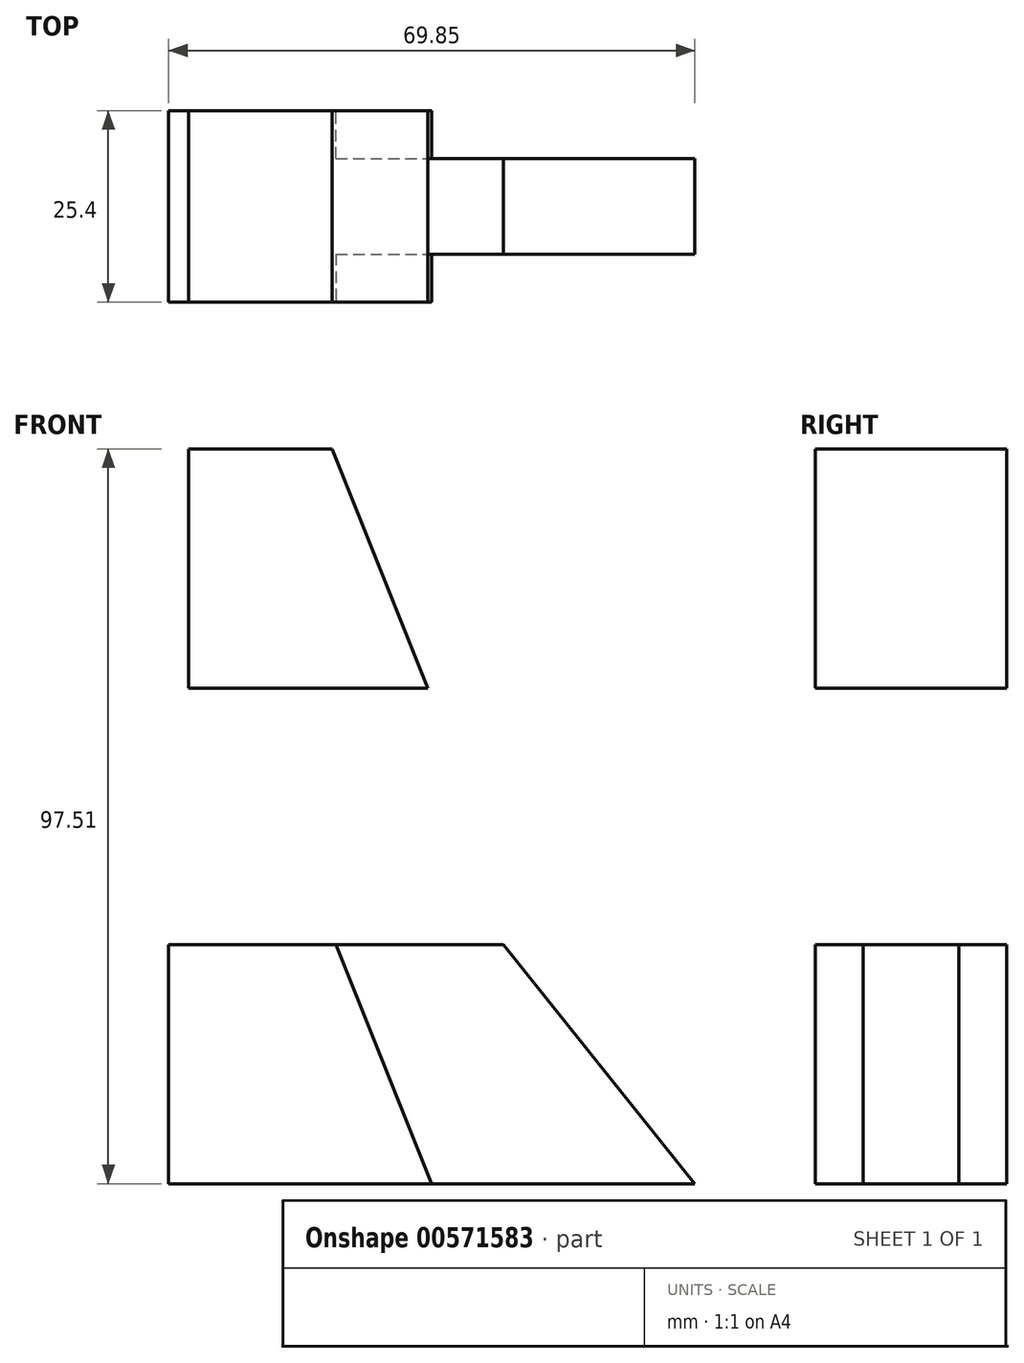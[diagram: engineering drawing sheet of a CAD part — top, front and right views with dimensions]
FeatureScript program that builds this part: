
annotation { "Feature Type Name" : "Feature", "Feature Type Description" : "" }
export const myFeature = defineFeature(function(context is Context, id is Id, definition is map)
    precondition{}
    {
        {
            var Q0;
            Q0=qCreatedBy(makeId("Front.planeOp"),FACE);
            var sketch = newSketch(context, id + "F0", { "sketchPlane" : qUnion([Q0])});
            skLineSegment(sketch, "E0", {"start": v(-62.13, 47.31) * mm, "end": v(-62.13, 15.56) * mm});
            skLineSegment(sketch, "E1", {"start": v(-62.13, 15.56) * mm, "end": v(-30.38, 15.56) * mm});
            skLineSegment(sketch, "E2", {"start": v(-62.13, 47.31) * mm, "end": v(-43.08, 47.31) * mm});
            skLineSegment(sketch, "E3", {"start": v(-43.08, 47.31) * mm, "end": v(-30.38, 15.56) * mm});
            skSolve(sketch);
        }
        {
            var Q0;
            Q0=makeQuery(id+"F0.imprint","IMPRINT",FACE,{"disambiguationData":[TD([[makeQuery(id+"F0.imprint","IMPRINT",EDGE,{"derivedFrom":sQuery(id+"F0.wireOp",EDGE,"E0")}),1.0]])]});
            extrude(context, id + "F1", {"entities" : qUnion([Q0]), "depth" : 25.4 * mm, "offsetDistance" : 25.4 * mm});
        }
        {
            var Q0;
            Q0=qCreatedBy(makeId("Front.planeOp"),FACE);
            var sketch = newSketch(context, id + "F2", { "sketchPlane" : qUnion([Q0])});
            skLineSegment(sketch, "E4", {"start": v(-64.78, -18.45) * mm, "end": v(-64.78, -50.2) * mm});
            skLineSegment(sketch, "E5", {"start": v(-64.78, -18.45) * mm, "end": v(-20.33, -18.45) * mm});
            skLineSegment(sketch, "E6", {"start": v(-64.78, -50.2) * mm, "end": v(5.07, -50.2) * mm});
            skLineSegment(sketch, "E7", {"start": v(-20.33, -18.45) * mm, "end": v(5.07, -50.2) * mm});
            skSolve(sketch);
        }
        {
            var Q0;
            Q0=makeQuery(id+"F2.imprint","IMPRINT",FACE,{"disambiguationData":[TD([[makeQuery(id+"F2.imprint","IMPRINT",EDGE,{"derivedFrom":sQuery(id+"F2.wireOp",EDGE,"E4")}),1.0]])]});
            extrude(context, id + "F3", {"entities" : qUnion([Q0]), "depth" : 25.4 * mm, "offsetDistance" : 25.4 * mm});
        }
        {
            var Q0;
            Q0=makeQuery(id+"F3.opExtrude","CAP_FACE",FACE,{"disambiguationData":[OSD([sQuery(id+"F2.wireOp",EDGE,"E4"),sQuery(id+"F2.wireOp",EDGE,"E5"),sQuery(id+"F2.wireOp",EDGE,"E6"),sQuery(id+"F2.wireOp",EDGE,"E7")])],"isStart":false});
            var sketch = newSketch(context, id + "F4", { "sketchPlane" : qUnion([Q0])});
            skLineSegment(sketch, "E8", {"start": v(-42.56, -18.45) * mm, "end": v(-29.86, -50.2) * mm});
            skSolve(sketch);
        }
        {
            var Q0;
            {var subQ0=sQuery(id+"F4.wireOp",EDGE,"E8");Q0=makeQuery(id+"F4.imprint","IMPRINT",FACE,{"disambiguationData":[TD([[makeQuery(id+"F4.imprint","IMPRINT",EDGE,{"derivedFrom":subQ0}),1.0]])]});}
            extrude(context, id + "F5", {"entities" : qUnion([Q0]), "operationType" : NewBodyOperationType.REMOVE, "oppositeDirection" : true, "depth" : 6.35 * mm, "offsetDistance" : 25.4 * mm});
        }
        {
            var Q0;
            Q0=makeQuery(id+"F3.opExtrude","CAP_FACE",FACE,{"disambiguationData":[OSD([sQuery(id+"F2.wireOp",EDGE,"E4"),sQuery(id+"F2.wireOp",EDGE,"E5"),sQuery(id+"F2.wireOp",EDGE,"E6"),sQuery(id+"F2.wireOp",EDGE,"E7")])],"isStart":true});
            var sketch = newSketch(context, id + "F6", { "sketchPlane" : qUnion([Q0])});
            skLineSegment(sketch, "E9", {"start": v(42.56, -18.45) * mm, "end": v(29.86, -50.2) * mm});
            skSolve(sketch);
        }
        {
            var Q0;
            {var subQ0=sQuery(id+"F6.wireOp",EDGE,"E9");Q0=makeQuery(id+"F6.imprint","IMPRINT",FACE,{"disambiguationData":[TD([[makeQuery(id+"F6.imprint","IMPRINT",EDGE,{"derivedFrom":subQ0}),-1.0]])]});}
            extrude(context, id + "F7", {"entities" : qUnion([Q0]), "operationType" : NewBodyOperationType.REMOVE, "oppositeDirection" : true, "depth" : 6.35 * mm, "offsetDistance" : 25.4 * mm});
        }
    });
